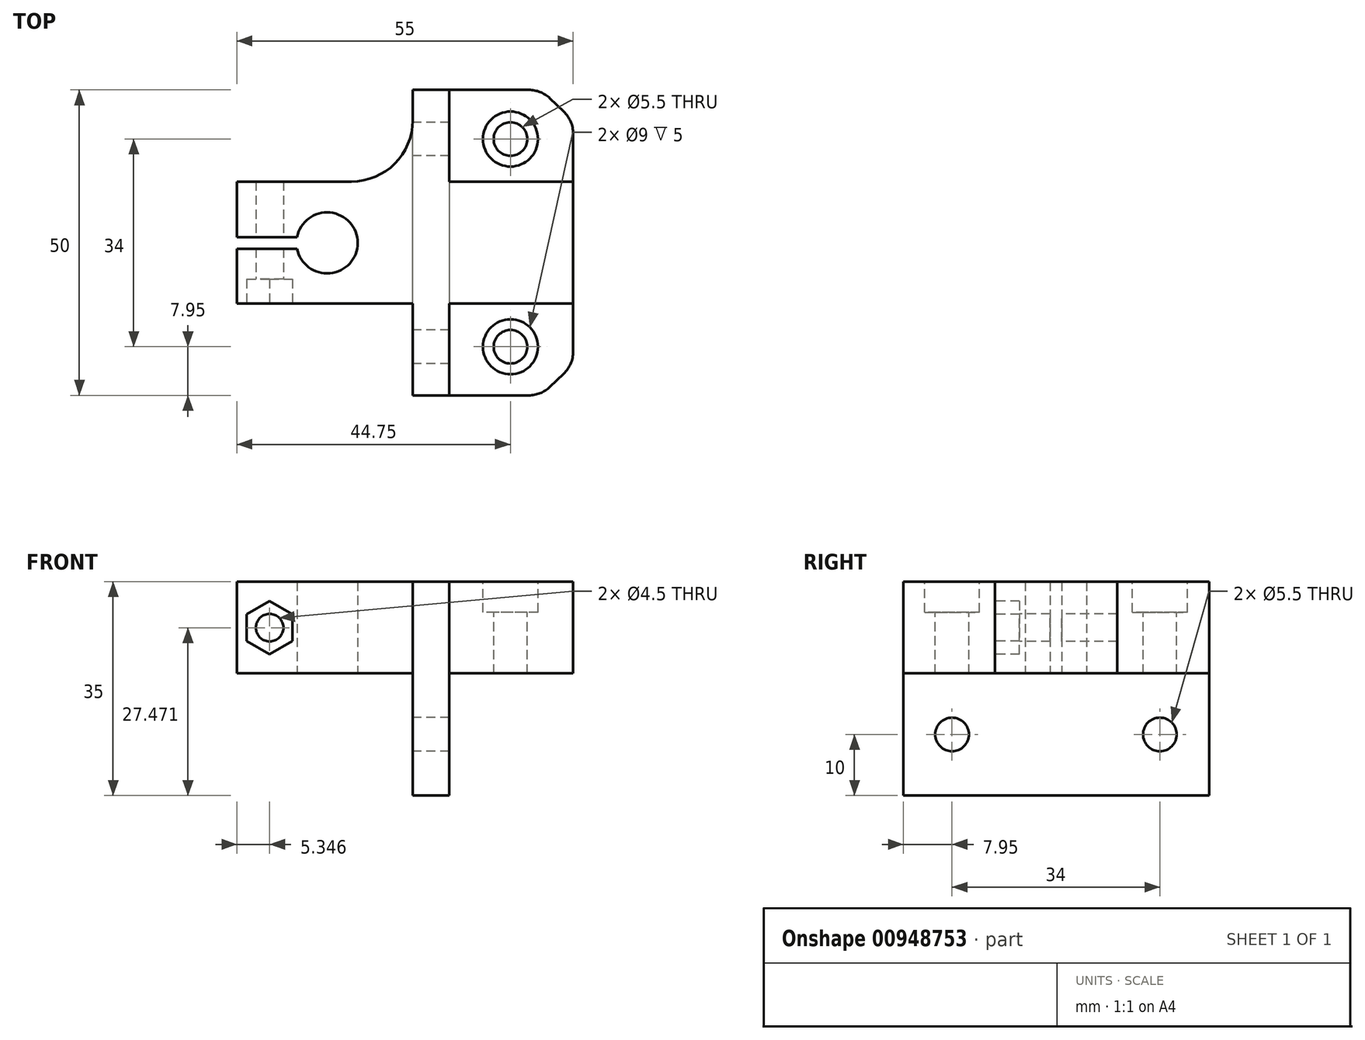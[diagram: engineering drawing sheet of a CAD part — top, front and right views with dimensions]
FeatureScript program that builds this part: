
annotation { "Feature Type Name" : "Feature", "Feature Type Description" : "" }
export const myFeature = defineFeature(function(context is Context, id is Id, definition is map)
    precondition{}
    {
        {
            var Q0;
            Q0=qCreatedBy(makeId("Top.planeOp"),FACE);
            var sketch = newSketch(context, id + "F0", { "sketchPlane" : qUnion([Q0])});
            skArc(sketch, "E0", {"start": v(-4.9, -0.95) * mm, "mid": v(5, 0) * mm, "end": v(-4.9, 0.95) * mm});
            skLineSegment(sketch, "E1", {"start": v(20.25, 0.05) * mm, "end": v(20.25, 25.44) * mm, "construction": true});
            skLineSegment(sketch, "E2", {"start": v(20.25, 0.05) * mm, "end": v(20.25, -26.28) * mm, "construction": true});
            skLineSegment(sketch, "E3", {"start": v(-14.75, 10.05) * mm, "end": v(40.25, 10.05) * mm});
            skLineSegment(sketch, "E4", {"start": v(-14.75, -9.95) * mm, "end": v(40.25, -9.95) * mm});
            skLineSegment(sketch, "E5", {"start": v(-14.75, 10.05) * mm, "end": v(-14.75, 0.95) * mm});
            skLineSegment(sketch, "E6", {"start": v(-14.75, 0.95) * mm, "end": v(-4.9, 0.95) * mm});
            skLineSegment(sketch, "E7", {"start": v(-14.75, -9.95) * mm, "end": v(-14.75, -0.95) * mm});
            skLineSegment(sketch, "E8", {"start": v(-14.75, -0.95) * mm, "end": v(-4.9, -0.95) * mm});
            skLineSegment(sketch, "E9", {"start": v(40.25, -9.95) * mm, "end": v(40.25, 10.05) * mm});
            skSolve(sketch);
        }
        {
            var Q0;
            Q0 = qSketchRegion(id + "F0", true);
            extrude(context, id + "F1", {"entities" : qUnion([Q0]), "depth" : 15 * mm, "offsetDistance" : 25 * mm});
        }
        {
            var Q0;
            Q0=makeQuery(id+"F1.opExtrude","SWEPT_FACE",FACE,{"disambiguationData":[OSD([sQuery(id+"F0.wireOp",EDGE,"E4")])]});
            var sketch = newSketch(context, id + "F2", { "sketchPlane" : qUnion([Q0])});
            skLineSegment(sketch, "E10", {"start": v(20, 15) * mm, "end": v(20, 0) * mm});
            skLineSegment(sketch, "E11", {"start": v(20, 0) * mm, "end": v(14, 0) * mm});
            skLineSegment(sketch, "E12", {"start": v(14, 0) * mm, "end": v(14, 15) * mm});
            skLineSegment(sketch, "E13", {"start": v(14, 15) * mm, "end": v(20, 15) * mm});
            skSolve(sketch);
        }
        {
            var Q0;
            Q0=makeQuery(id+"F2.imprint","IMPRINT",FACE,{"disambiguationData":[TD([[makeQuery(id+"F2.imprint","IMPRINT",EDGE,{"derivedFrom":sQuery(id+"F2.wireOp",EDGE,"E10")}),-1.0]])]});
            extrude(context, id + "F3", {"entities" : qUnion([Q0]), "operationType" : NewBodyOperationType.ADD, "depth" : 15 * mm, "offsetDistance" : 25 * mm});
        }
        {
            var Q0;
            Q0=makeQuery(id+"F1.opExtrude","SWEPT_FACE",FACE,{"disambiguationData":[OSD([sQuery(id+"F0.wireOp",EDGE,"E3")])]});
            var sketch = newSketch(context, id + "F4", { "sketchPlane" : qUnion([Q0])});
            skLineSegment(sketch, "E14", {"start": v(-20, 15) * mm, "end": v(-20, 0) * mm});
            skLineSegment(sketch, "E15", {"start": v(-20, 0) * mm, "end": v(-14, 0) * mm});
            skLineSegment(sketch, "E16", {"start": v(-14, 0) * mm, "end": v(-14, 15) * mm});
            skLineSegment(sketch, "E17", {"start": v(-14, 15) * mm, "end": v(-20, 15) * mm});
            skSolve(sketch);
        }
        {
            var Q0;
            Q0=makeQuery(id+"F4.imprint","IMPRINT",FACE,{"disambiguationData":[TD([[makeQuery(id+"F4.imprint","IMPRINT",EDGE,{"derivedFrom":sQuery(id+"F4.wireOp",EDGE,"E14")}),1.0]])]});
            extrude(context, id + "F5", {"entities" : qUnion([Q0]), "operationType" : NewBodyOperationType.ADD, "depth" : 15 * mm, "offsetDistance" : 25 * mm});
        }
        {
            var Q0;
            Q0=makeQuery(id+"F5.boolean.opBoolean","MERGE",FACE,{"derivedFrom":[makeQuery(id+"F3.boolean.opBoolean","MERGE",FACE,{"derivedFrom":[makeQuery(id+"F1.opExtrude","CAP_FACE",FACE,{"disambiguationData":[OSD([sQuery(id+"F0.wireOp",EDGE,"E0"),sQuery(id+"F0.wireOp",EDGE,"E3"),sQuery(id+"F0.wireOp",EDGE,"E4"),sQuery(id+"F0.wireOp",EDGE,"E5"),sQuery(id+"F0.wireOp",EDGE,"E6"),sQuery(id+"F0.wireOp",EDGE,"E7"),sQuery(id+"F0.wireOp",EDGE,"E8"),sQuery(id+"F0.wireOp",EDGE,"E9")])],"isStart":true}),makeQuery(id+"F3.opExtrude","SWEPT_FACE",FACE,{"disambiguationData":[OSD([sQuery(id+"F2.wireOp",EDGE,"E11")])]})]}),makeQuery(id+"F5.opExtrude","SWEPT_FACE",FACE,{"disambiguationData":[OSD([sQuery(id+"F4.wireOp",EDGE,"E15")])]})]});
            var sketch = newSketch(context, id + "F6", { "sketchPlane" : qUnion([Q0])});
            skLineSegment(sketch, "E18.bottom", {"start": v(14, 24.95) * mm, "end": v(20, 24.95) * mm});
            skLineSegment(sketch, "E18.top", {"start": v(14, -25.05) * mm, "end": v(20, -25.05) * mm});
            skLineSegment(sketch, "E18.left", {"start": v(14, 24.95) * mm, "end": v(14, -25.05) * mm});
            skLineSegment(sketch, "E18.right", {"start": v(20, 24.95) * mm, "end": v(20, -25.05) * mm});
            skSolve(sketch);
        }
        {
            var Q0;
            Q0 = qSketchRegion(id + "F6", true);
            extrude(context, id + "F7", {"entities" : qUnion([Q0]), "operationType" : NewBodyOperationType.ADD, "depth" : 20 * mm, "offsetDistance" : 25 * mm});
        }
        {
            var Q0;
            Q0=makeQuery(id+"F7.boolean.opBoolean","MERGE",FACE,{"derivedFrom":[makeQuery(id+"F3.opExtrude","SWEPT_FACE",FACE,{"disambiguationData":[OSD([sQuery(id+"F2.wireOp",EDGE,"E12")])]}),makeQuery(id+"F5.opExtrude","SWEPT_FACE",FACE,{"disambiguationData":[OSD([sQuery(id+"F4.wireOp",EDGE,"E16")])]}),makeQuery(id+"F7.opExtrude","SWEPT_FACE",FACE,{"disambiguationData":[OSD([sQuery(id+"F6.wireOp",EDGE,"E18.left")])]})]});
            var sketch = newSketch(context, id + "F8", { "sketchPlane" : qUnion([Q0])});
            skCircle(sketch, "E19", {"center": v(-17, -10) * mm, "radius": 2.75 * mm});
            skCircle(sketch, "E20", {"center": v(17, -10) * mm, "radius": 2.75 * mm});
            skSolve(sketch);
        }
        {
            var Q0;
            Q0=makeQuery(id+"F8.imprint","IMPRINT",FACE,{"disambiguationData":[TD([[makeQuery(id+"F8.imprint","IMPRINT",EDGE,{"derivedFrom":sQuery(id+"F8.wireOp",EDGE,"E19")}),1.0]])]});
            var Q1;
            Q1=makeQuery(id+"F8.imprint","IMPRINT",FACE,{"disambiguationData":[TD([[makeQuery(id+"F8.imprint","IMPRINT",EDGE,{"derivedFrom":sQuery(id+"F8.wireOp",EDGE,"E20")}),1.0]])]});
            extrude(context, id + "F9", {"entities" : qUnion([Q0, Q1]), "operationType" : NewBodyOperationType.REMOVE, "oppositeDirection" : true, "depth" : 10 * mm, "offsetDistance" : 25 * mm});
        }
        {
            var Q0;
            Q0=makeQuery(id+"F5.boolean.opBoolean","MERGE",FACE,{"derivedFrom":[makeQuery(id+"F3.boolean.opBoolean","MERGE",FACE,{"derivedFrom":[makeQuery(id+"F1.opExtrude","CAP_FACE",FACE,{"disambiguationData":[OSD([sQuery(id+"F0.wireOp",EDGE,"E0"),sQuery(id+"F0.wireOp",EDGE,"E3"),sQuery(id+"F0.wireOp",EDGE,"E4"),sQuery(id+"F0.wireOp",EDGE,"E5"),sQuery(id+"F0.wireOp",EDGE,"E6"),sQuery(id+"F0.wireOp",EDGE,"E7"),sQuery(id+"F0.wireOp",EDGE,"E8"),sQuery(id+"F0.wireOp",EDGE,"E9")])],"isStart":false}),makeQuery(id+"F3.opExtrude","SWEPT_FACE",FACE,{"disambiguationData":[OSD([sQuery(id+"F2.wireOp",EDGE,"E13")])]})]}),makeQuery(id+"F5.opExtrude","SWEPT_FACE",FACE,{"disambiguationData":[OSD([sQuery(id+"F4.wireOp",EDGE,"E17")])]})]});
            var sketch = newSketch(context, id + "F10", { "sketchPlane" : qUnion([Q0])});
            skLineSegment(sketch, "E21", {"start": v(20, 10.05) * mm, "end": v(20, 25.05) * mm});
            skLineSegment(sketch, "E22", {"start": v(20, 25.05) * mm, "end": v(35, 25.05) * mm});
            skLineSegment(sketch, "E23", {"start": v(40.25, 10.05) * mm, "end": v(40.25, 20.05) * mm});
            skLineSegment(sketch, "E24", {"start": v(40.25, 20.05) * mm, "end": v(35, 25.05) * mm});
            skLineSegment(sketch, "E25", {"start": v(20, -9.95) * mm, "end": v(20, -24.95) * mm});
            skLineSegment(sketch, "E26", {"start": v(20, -24.95) * mm, "end": v(35, -24.95) * mm});
            skLineSegment(sketch, "E27", {"start": v(40.25, -9.95) * mm, "end": v(40.25, -19.95) * mm});
            skLineSegment(sketch, "E28", {"start": v(40.25, -19.95) * mm, "end": v(35, -24.95) * mm});
            skSolve(sketch);
        }
        {
            var Q0;
            Q0=makeQuery(id+"F10.imprint","IMPRINT",FACE,{"disambiguationData":[TD([[makeQuery(id+"F10.imprint","IMPRINT",EDGE,{"derivedFrom":sQuery(id+"F10.wireOp",EDGE,"E21")}),1.0]])]});
            var Q1;
            Q1=makeQuery(id+"F10.imprint","IMPRINT",FACE,{"disambiguationData":[TD([[makeQuery(id+"F10.imprint","IMPRINT",EDGE,{"derivedFrom":sQuery(id+"F10.wireOp",EDGE,"E25")}),-1.0]])]});
            extrude(context, id + "F11", {"entities" : qUnion([Q0, Q1]), "oppositeDirection" : true, "depth" : 15 * mm, "offsetDistance" : 25 * mm});
        }
        {
            var Q0;
            Q0=makeQuery(id+"F3.opExtrude","CAP_EDGE",EDGE,{"disambiguationData":[OSD([sQuery(id+"F2.wireOp",EDGE,"E12")])],"isStart":true});
            var Q1;
            Q1=makeQuery(id+"F5.opExtrude","CAP_EDGE",EDGE,{"disambiguationData":[OSD([sQuery(id+"F4.wireOp",EDGE,"E16")])],"isStart":true});
            fillet(context, id + "F12", {"entities" : qUnion([Q0, Q1]), "radius" : 10 * mm, "tangentPropagation" : true, "allowEdgeOverflow" : false});
        }
        {
            var Q0;
            Q0=makeQuery(id+"F11.opExtrude","SWEPT_EDGE",EDGE,{"disambiguationData":[OSD([sQuery(id+"F10.wireOp",EDGE,"E26"),sQuery(id+"F10.wireOp",EDGE,"E28")])]});
            var Q1;
            Q1=makeQuery(id+"F11.opExtrude","SWEPT_EDGE",EDGE,{"disambiguationData":[OSD([sQuery(id+"F10.wireOp",EDGE,"E27"),sQuery(id+"F10.wireOp",EDGE,"E28")])]});
            var Q2;
            Q2=makeQuery(id+"F11.opExtrude","SWEPT_EDGE",EDGE,{"disambiguationData":[OSD([sQuery(id+"F10.wireOp",EDGE,"E23"),sQuery(id+"F10.wireOp",EDGE,"E24")])]});
            var Q3;
            Q3=makeQuery(id+"F11.opExtrude","SWEPT_EDGE",EDGE,{"disambiguationData":[OSD([sQuery(id+"F10.wireOp",EDGE,"E22"),sQuery(id+"F10.wireOp",EDGE,"E24")])]});
            fillet(context, id + "F13", {"entities" : qUnion([Q0, Q1, Q2, Q3]), "radius" : 5 * mm, "tangentPropagation" : true, "allowEdgeOverflow" : false});
        }
        {
            var Q0;
            {var subQ0=sQuery(id+"F0.wireOp",EDGE,"E7");var subQ5=sQuery(id+"F0.wireOp",EDGE,"E4");Q0=makeQuery(id+"F3.boolean.opBoolean","SPLIT",FACE,{"disambiguationData":[TD([makeQuery(id+"F1.opExtrude","SWEPT_FACE",FACE,{"disambiguationData":[OSD([subQ0])]})])],"derivedFrom":makeQuery(id+"F1.opExtrude","SWEPT_FACE",FACE,{"disambiguationData":[OSD([subQ5])]})});}
            var sketch = newSketch(context, id + "F14", { "sketchPlane" : qUnion([Q0])});
            skCircle(sketch, "E29", {"center": v(-9.4, 7.47) * mm, "radius": 2.25 * mm});
            skPoint(sketch, "E30.0.midPoint", {"position": v(-5.4, 7.47) * mm});
            skLineSegment(sketch, "E31.0", {"start": v(-5.65, 9.64) * mm, "end": v(-5.65, 5.3) * mm});
            skLineSegment(sketch, "E31.1", {"start": v(-5.65, 5.3) * mm, "end": v(-9.4, 3.14) * mm});
            skLineSegment(sketch, "E31.2", {"start": v(-9.4, 3.14) * mm, "end": v(-13.15, 5.3) * mm});
            skLineSegment(sketch, "E31.3", {"start": v(-13.15, 5.3) * mm, "end": v(-13.15, 9.64) * mm});
            skLineSegment(sketch, "E31.4", {"start": v(-13.15, 9.64) * mm, "end": v(-9.4, 11.8) * mm});
            skLineSegment(sketch, "E31.5", {"start": v(-9.4, 11.8) * mm, "end": v(-5.65, 9.64) * mm});
            skPoint(sketch, "E31.0.midPoint", {"position": v(-5.65, 7.47) * mm});
            skSolve(sketch);
        }
        {
            var Q0;
            Q0=makeQuery(id+"F14.imprint","IMPRINT",FACE,{"disambiguationData":[TD([[makeQuery(id+"F14.imprint","IMPRINT",EDGE,{"derivedFrom":sQuery(id+"F14.wireOp",EDGE,"E29")}),1.0]])]});
            extrude(context, id + "F15", {"entities" : qUnion([Q0]), "operationType" : NewBodyOperationType.REMOVE, "oppositeDirection" : true, "depth" : 25 * mm, "offsetDistance" : 25 * mm});
        }
        {
            var Q0;
            Q0=makeQuery(id+"F11.opExtrude","CAP_FACE",FACE,{"disambiguationData":[OSD([sQuery(id+"F0.wireOp",EDGE,"E3"),sQuery(id+"F10.wireOp",EDGE,"E21"),sQuery(id+"F10.wireOp",EDGE,"E22"),sQuery(id+"F10.wireOp",EDGE,"E23"),sQuery(id+"F10.wireOp",EDGE,"E24")])],"isStart":true});
            var sketch = newSketch(context, id + "F16", { "sketchPlane" : qUnion([Q0])});
            skCircle(sketch, "E32", {"center": v(30, 17) * mm, "radius": 2.75 * mm});
            skCircle(sketch, "E33", {"center": v(30, 17) * mm, "radius": 4.5 * mm});
            skSolve(sketch);
        }
        {
            var Q0;
            Q0=makeQuery(id+"F16.imprint","IMPRINT",FACE,{"disambiguationData":[TD([[makeQuery(id+"F16.imprint","IMPRINT",EDGE,{"derivedFrom":sQuery(id+"F16.wireOp",EDGE,"E32")}),1.0]])]});
            extrude(context, id + "F17", {"entities" : qUnion([Q0]), "operationType" : NewBodyOperationType.REMOVE, "oppositeDirection" : true, "depth" : 20 * mm, "offsetDistance" : 25 * mm});
        }
        {
            var Q0;
            Q0=makeQuery(id+"F16.imprint","IMPRINT",FACE,{"disambiguationData":[TD([[makeQuery(id+"F16.imprint","IMPRINT",EDGE,{"derivedFrom":sQuery(id+"F16.wireOp",EDGE,"E32")}),-1.0]])]});
            extrude(context, id + "F18", {"entities" : qUnion([Q0]), "operationType" : NewBodyOperationType.REMOVE, "oppositeDirection" : true, "depth" : 5 * mm, "offsetDistance" : 25 * mm});
        }
        {
            var Q0;
            Q0=makeQuery(id+"F11.opExtrude","CAP_FACE",FACE,{"disambiguationData":[OSD([sQuery(id+"F0.wireOp",EDGE,"E4"),sQuery(id+"F10.wireOp",EDGE,"E25"),sQuery(id+"F10.wireOp",EDGE,"E26"),sQuery(id+"F10.wireOp",EDGE,"E27"),sQuery(id+"F10.wireOp",EDGE,"E28")])],"isStart":true});
            var sketch = newSketch(context, id + "F19", { "sketchPlane" : qUnion([Q0])});
            skCircle(sketch, "E34", {"center": v(30, -17) * mm, "radius": 2.75 * mm});
            skCircle(sketch, "E35", {"center": v(30, -17) * mm, "radius": 4.5 * mm});
            skSolve(sketch);
        }
        {
            var Q0;
            Q0=makeQuery(id+"F19.imprint","IMPRINT",FACE,{"disambiguationData":[TD([[makeQuery(id+"F19.imprint","IMPRINT",EDGE,{"derivedFrom":sQuery(id+"F19.wireOp",EDGE,"E34")}),1.0]])]});
            extrude(context, id + "F20", {"entities" : qUnion([Q0]), "operationType" : NewBodyOperationType.REMOVE, "oppositeDirection" : true, "depth" : 20 * mm, "offsetDistance" : 25 * mm});
        }
        {
            var Q0;
            Q0=makeQuery(id+"F19.imprint","IMPRINT",FACE,{"disambiguationData":[TD([[makeQuery(id+"F19.imprint","IMPRINT",EDGE,{"derivedFrom":sQuery(id+"F19.wireOp",EDGE,"E34")}),-1.0]])]});
            extrude(context, id + "F21", {"entities" : qUnion([Q0]), "operationType" : NewBodyOperationType.REMOVE, "oppositeDirection" : true, "depth" : 5 * mm, "offsetDistance" : 25 * mm});
        }
        {
            var Q0;
            Q0=makeQuery(id+"F14.imprint","IMPRINT",FACE,{"disambiguationData":[TD([[makeQuery(id+"F14.imprint","IMPRINT",EDGE,{"derivedFrom":sQuery(id+"F14.wireOp",EDGE,"E29")}),-1.0]])]});
            extrude(context, id + "F22", {"entities" : qUnion([Q0]), "operationType" : NewBodyOperationType.REMOVE, "oppositeDirection" : true, "depth" : 4 * mm, "offsetDistance" : 25 * mm});
        }
    });
